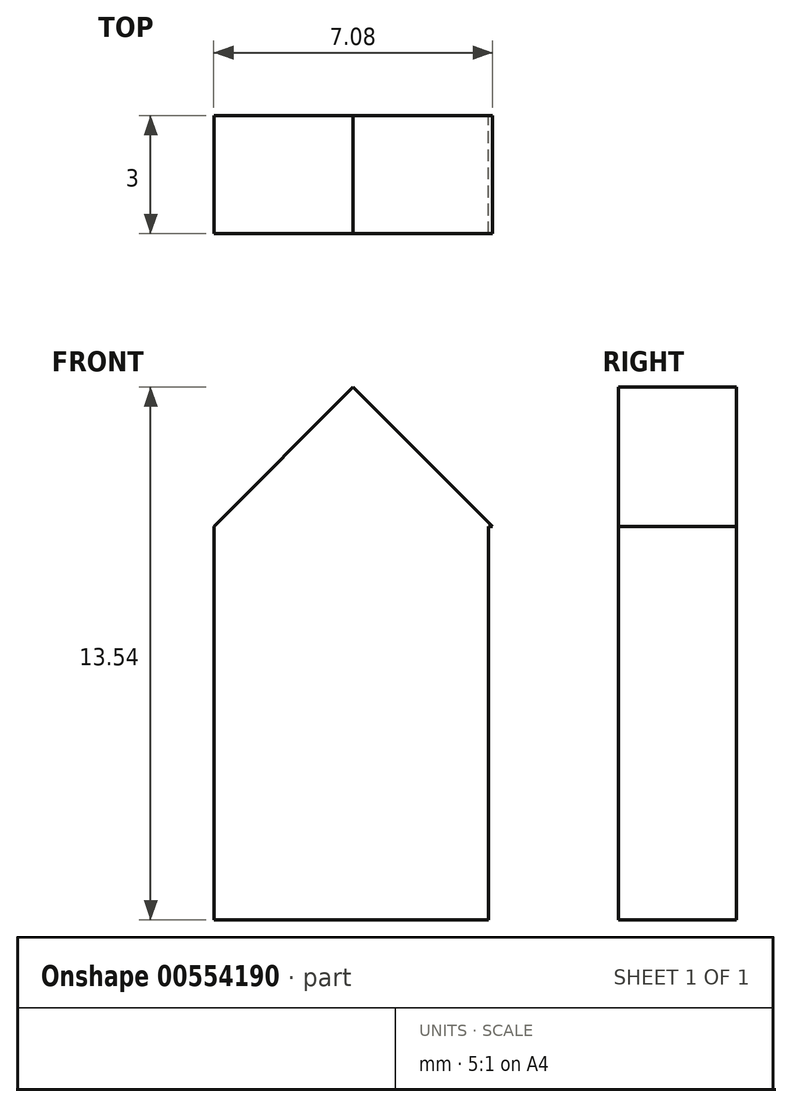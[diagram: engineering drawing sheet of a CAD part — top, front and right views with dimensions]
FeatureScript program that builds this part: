
annotation { "Feature Type Name" : "Feature", "Feature Type Description" : "" }
export const myFeature = defineFeature(function(context is Context, id is Id, definition is map)
    precondition{}
    {
        {
            var Q0;
            Q0=qCreatedBy(makeId("Front.planeOp"),FACE);
            var sketch = newSketch(context, id + "F0", { "sketchPlane" : qUnion([Q0])});
            skLineSegment(sketch, "E0", {"start": v(0, 0) * mm, "end": v(-3.54, 0) * mm});
            skLineSegment(sketch, "E1", {"start": v(-3.54, 0) * mm, "end": v(0, 3.54) * mm});
            skLineSegment(sketch, "E2", {"start": v(0, 3.54) * mm, "end": v(3.54, 0) * mm});
            skLineSegment(sketch, "E3", {"start": v(3.54, 0) * mm, "end": v(0, 0) * mm});
            skLineSegment(sketch, "E4", {"start": v(-3.54, 0) * mm, "end": v(-3.54, -10) * mm});
            skLineSegment(sketch, "E5", {"start": v(-3.54, -10) * mm, "end": v(3.44, -10) * mm});
            skLineSegment(sketch, "E6", {"start": v(3.44, -10) * mm, "end": v(3.44, 0) * mm});
            skLineSegment(sketch, "E7", {"start": v(3.54, 0) * mm, "end": v(3.44, 0) * mm});
            skSolve(sketch);
        }
        {
            var Q0;
            Q0=makeQuery(id+"F0.imprint","IMPRINT",FACE,{"disambiguationData":[TD([[makeQuery(id+"F0.imprint","IMPRINT",EDGE,{"derivedFrom":sQuery(id+"F0.wireOp",EDGE,"E0")}),1.0]])]});
            var Q1;
            Q1=makeQuery(id+"F0.imprint","IMPRINT",FACE,{"disambiguationData":[TD([[makeQuery(id+"F0.imprint","IMPRINT",EDGE,{"derivedFrom":sQuery(id+"F0.wireOp",EDGE,"E0")}),-1.0]])]});
            extrude(context, id + "F1", {"entities" : qUnion([Q0, Q1]), "depth" : 3 * mm, "offsetDistance" : 25 * mm});
        }
    });
